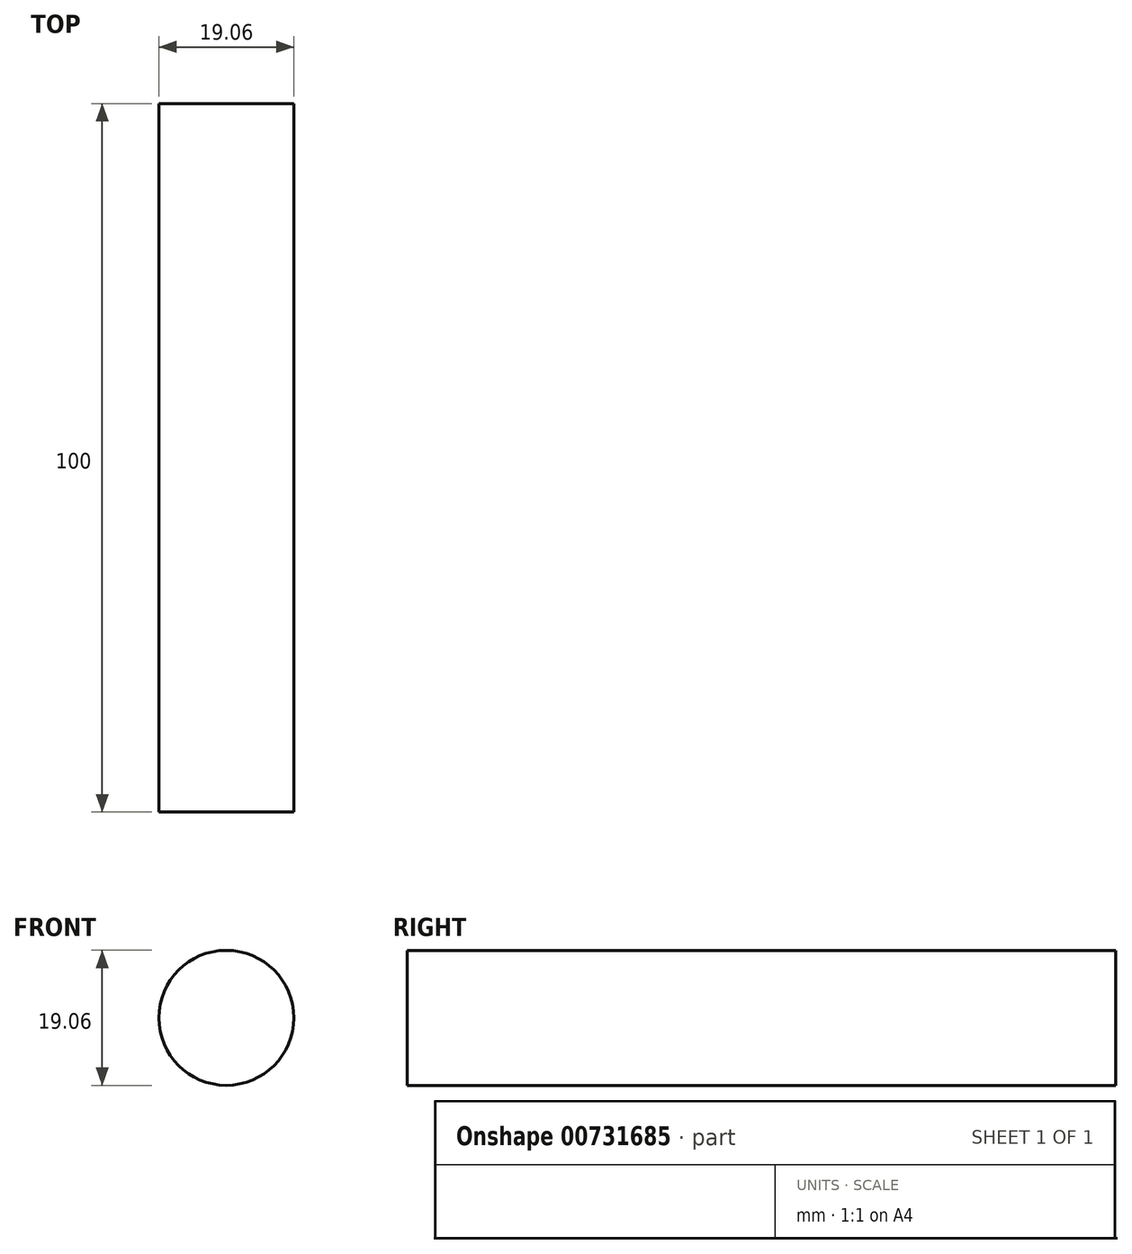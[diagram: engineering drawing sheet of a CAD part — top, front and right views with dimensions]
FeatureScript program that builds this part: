
annotation { "Feature Type Name" : "Feature", "Feature Type Description" : "" }
export const myFeature = defineFeature(function(context is Context, id is Id, definition is map)
    precondition{}
    {
        {
            var Q0;
            Q0=qCreatedBy(makeId("Front.planeOp"),FACE);
            var sketch = newSketch(context, id + "F0", { "sketchPlane" : qUnion([Q0])});
            skCircle(sketch, "E0", {"center": v(0, 0) * mm, "radius": 9.53 * mm});
            skSolve(sketch);
        }
        {
            var Q0;
            Q0=makeQuery(id+"F0.imprint","IMPRINT",FACE,{"disambiguationData":[TD([[makeQuery(id+"F0.imprint","IMPRINT",EDGE,{"derivedFrom":sQuery(id+"F0.wireOp",EDGE,"E0")}),1.0]])]});
            extrude(context, id + "F1", {"entities" : qUnion([Q0]), "depth" : 100 * mm, "offsetDistance" : 25.4 * mm});
        }
    });
